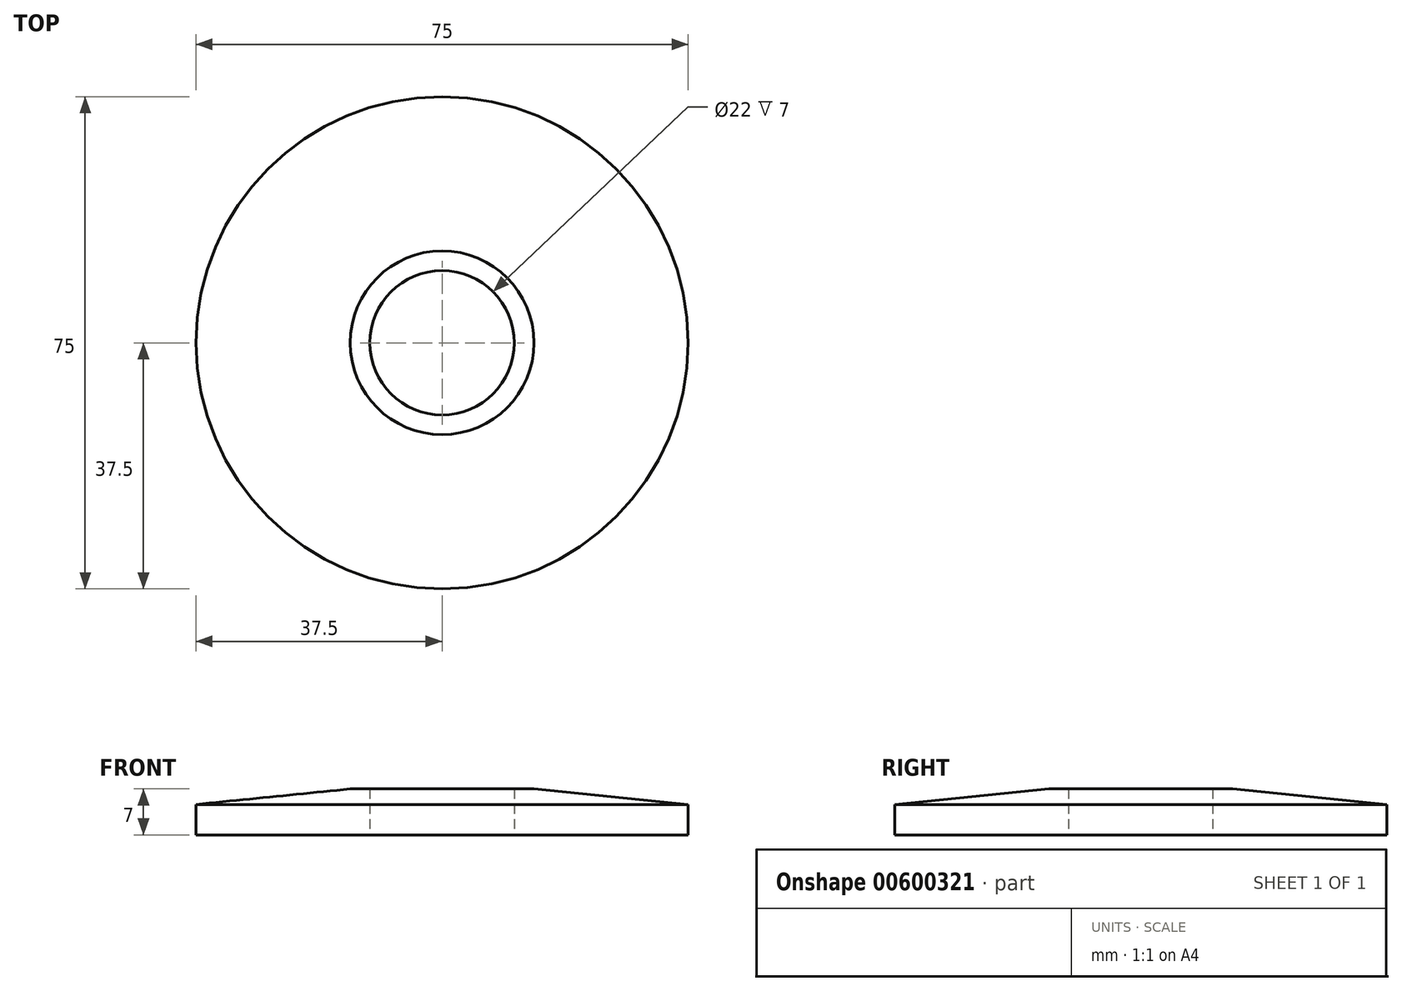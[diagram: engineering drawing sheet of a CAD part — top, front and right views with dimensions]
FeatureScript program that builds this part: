
annotation { "Feature Type Name" : "Feature", "Feature Type Description" : "" }
export const myFeature = defineFeature(function(context is Context, id is Id, definition is map)
    precondition{}
    {
        {
            var Q0;
            Q0=qCreatedBy(makeId("Top.planeOp"),FACE);
            var sketch = newSketch(context, id + "F0", { "sketchPlane" : qUnion([Q0])});
            skCircle(sketch, "E0", {"center": v(0, 0) * mm, "radius": 11 * mm});
            skCircle(sketch, "E1", {"center": v(0, 0) * mm, "radius": 37.5 * mm});
            skSolve(sketch);
        }
        {
            var Q0;
            Q0 = qSketchRegion(id + "F0", true);
            extrude(context, id + "F1", {"entities" : qUnion([Q0]), "endBound" : BoundingType.SYMMETRIC, "depth" : 7 * mm, "offsetDistance" : 25 * mm});
        }
        {
            var Q0;
            Q0=qCreatedBy(makeId("Right.planeOp"),FACE);
            var sketch = newSketch(context, id + "F2", { "sketchPlane" : qUnion([Q0])});
            skLineSegment(sketch, "E2", {"start": v(43.86, 0) * mm, "end": v(43.86, 0.5) * mm});
            skLineSegment(sketch, "E3", {"start": v(43.86, 0.5) * mm, "end": v(14, 3.5) * mm});
            skLineSegment(sketch, "E4", {"start": v(14, 3.5) * mm, "end": v(14, 16.89) * mm});
            skLineSegment(sketch, "E5", {"start": v(14, 16.89) * mm, "end": v(53.18, 16.89) * mm});
            skLineSegment(sketch, "E6", {"start": v(53.18, 16.89) * mm, "end": v(53.18, 0) * mm});
            skLineSegment(sketch, "E7", {"start": v(53.18, 0) * mm, "end": v(43.86, 0) * mm});
            skLineSegment(sketch, "E8.0", {"start": v(-11, 3.5) * mm, "end": v(11, 3.5) * mm, "construction": true});
            skLineSegment(sketch, "E9", {"start": v(0, 0) * mm, "end": v(0, 24.2) * mm, "construction": true});
            skSolve(sketch);
        }
        {
            var Q0;
            Q0 = qSketchRegion(id + "F2", true);
            var Q1;
            Q1=sQuery(id+"F2.wireOp",EDGE,"E9");
            revolve(context, id + "F3", {"operationType" : NewBodyOperationType.REMOVE, "surfaceOperationType" : NewSurfaceOperationType.NEW, "entities" : qUnion([Q0]), "axis" : qUnion([Q1]), "revolveType" : RevolveType.FULL, "oppositeDirection" : true});
        }
    });
